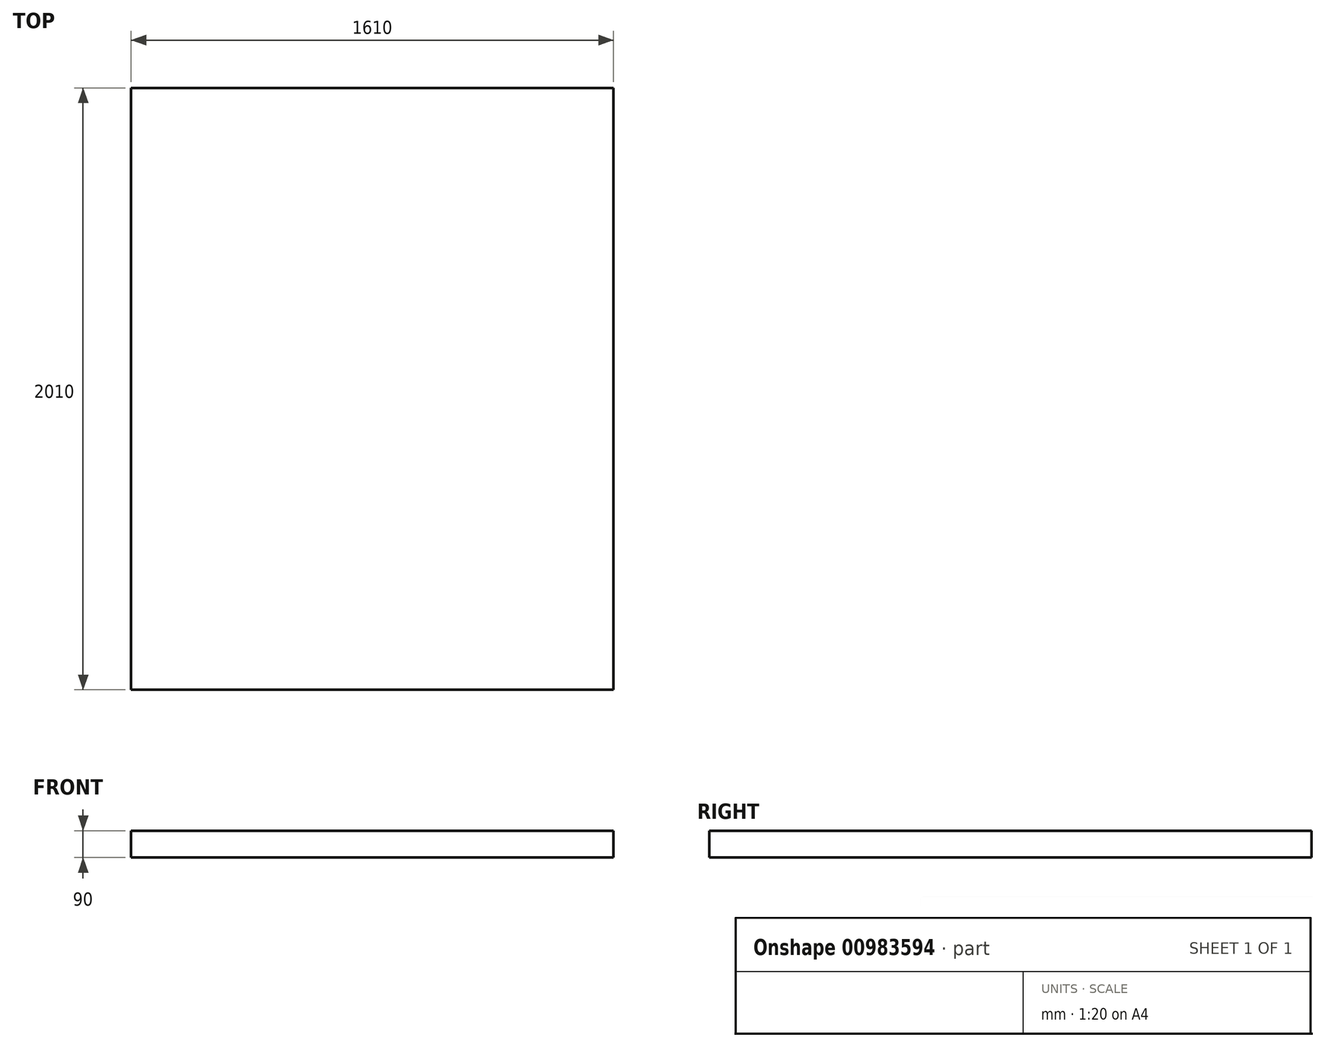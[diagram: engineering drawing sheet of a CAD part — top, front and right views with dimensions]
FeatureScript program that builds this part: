
annotation { "Feature Type Name" : "Feature", "Feature Type Description" : "" }
export const myFeature = defineFeature(function(context is Context, id is Id, definition is map)
    precondition{}
    {
        {
            var Q0;
            Q0=qCreatedBy(makeId("Top.planeOp"),FACE);
            var sketch = newSketch(context, id + "F0", { "sketchPlane" : qUnion([Q0])});
            skLineSegment(sketch, "E0.bottom", {"start": v(-805, 1005) * mm, "end": v(805, 1005) * mm});
            skLineSegment(sketch, "E0.top", {"start": v(-805, -1005) * mm, "end": v(805, -1005) * mm});
            skLineSegment(sketch, "E0.left", {"start": v(-805, 1005) * mm, "end": v(-805, -1005) * mm});
            skLineSegment(sketch, "E0.right", {"start": v(805, 1005) * mm, "end": v(805, -1005) * mm});
            skPoint(sketch, "E0.middle", {"position": v(0, 0) * mm});
            skSolve(sketch);
        }
        {
            var Q0;
            Q0=makeQuery(id+"F0.imprint","IMPRINT",FACE,{"disambiguationData":[TD([[makeQuery(id+"F0.imprint","IMPRINT",EDGE,{"derivedFrom":sQuery(id+"F0.wireOp",EDGE,"E0.bottom")}),-1.0]])]});
            extrude(context, id + "F1", {"entities" : qUnion([Q0]), "depth" : 90 * mm, "offsetDistance" : 25 * mm});
        }
    });
